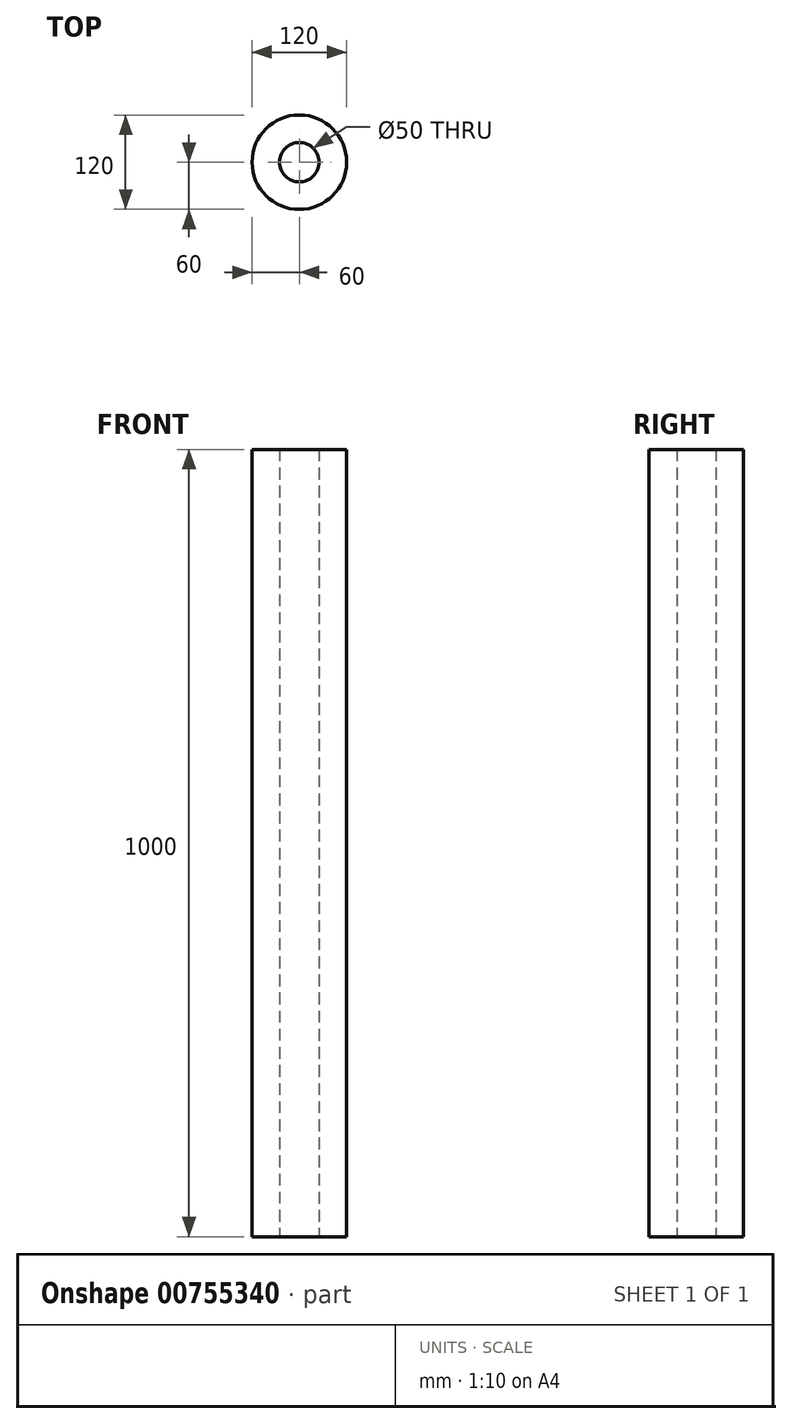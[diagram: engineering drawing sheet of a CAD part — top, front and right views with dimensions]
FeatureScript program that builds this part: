
annotation { "Feature Type Name" : "Feature", "Feature Type Description" : "" }
export const myFeature = defineFeature(function(context is Context, id is Id, definition is map)
    precondition{}
    {
        {
            var Q0;
            Q0=qCreatedBy(makeId("Top.planeOp"),FACE);
            var sketch = newSketch(context, id + "F0", { "sketchPlane" : qUnion([Q0])});
            skCircle(sketch, "E0", {"center": v(0, 0) * mm, "radius": 60 * mm});
            skCircle(sketch, "E1", {"center": v(0, 0) * mm, "radius": 25 * mm});
            skLineSegment(sketch, "E2", {"start": v(60, 0) * mm, "end": v(-1663.77, 551.65) * mm});
            skSolve(sketch);
        }
        {
            var Q0;
            Q0=makeQuery(id+"F0.imprint","IMPRINT",FACE,{"disambiguationData":[TD([[makeQuery(id+"F0.imprint","IMPRINT",EDGE,{"derivedFrom":sQuery(id+"F0.wireOp",EDGE,"E0")}),1.0]])]});
            extrude(context, id + "F1", {"entities" : qUnion([Q0]), "endBound" : BoundingType.SYMMETRIC, "depth" : 1000 * mm, "offsetDistance" : 25 * mm});
        }
    });
